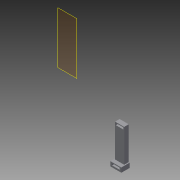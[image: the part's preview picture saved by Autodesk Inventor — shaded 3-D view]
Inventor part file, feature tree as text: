
AUTODESK INVENTOR PART (.ipt)
format: ipt  version: 2015 (Build 190159000, 159)  size: 133,120 bytes
history: native  units: in
note: dims shown in document units (in); Inventor stores cm internally (conversion verified against a paired STEP export)
features: extrude x4, sketch x4, reference x2, projected_geometry x2, plane x1
ambient origin geometry x8: Origin, YZ Plane, XZ Plane, XY Plane, X Axis, Y Axis, Z Axis, Center Point
bodies: Solid1 (feature_tree)
feature tree (13):
  plane  "Work Plane1"
  extrude  "Extrusion1"  Depth=0.1in TaperAngle=0.0deg
  extrude  "Extrusion2"  Depth=0.125in
  extrude  "Extrusion3"  Depth=0.125in
  extrude  "Extrusion4"  Depth=0.5in TaperAngle=0.0deg
  sketch  "Sketch1"  dims[d2=0.5in d3=0.0in d4=0.1in d5=0.0in]
  reference  "Reference1"
  reference  "Reference2"
  sketch  "Sketch2"  dims[d6=0.125in d9=0.125in]
  sketch  "Sketch3"  dims[d10=0.125in d11=0.125in]
  projected_geometry  "Projected Loop1"
  sketch  "Sketch4"  dims[d12=0.625in d13=0.0in d14=0.5in d15=0.0in]
  projected_geometry  "Projected Loop2"
